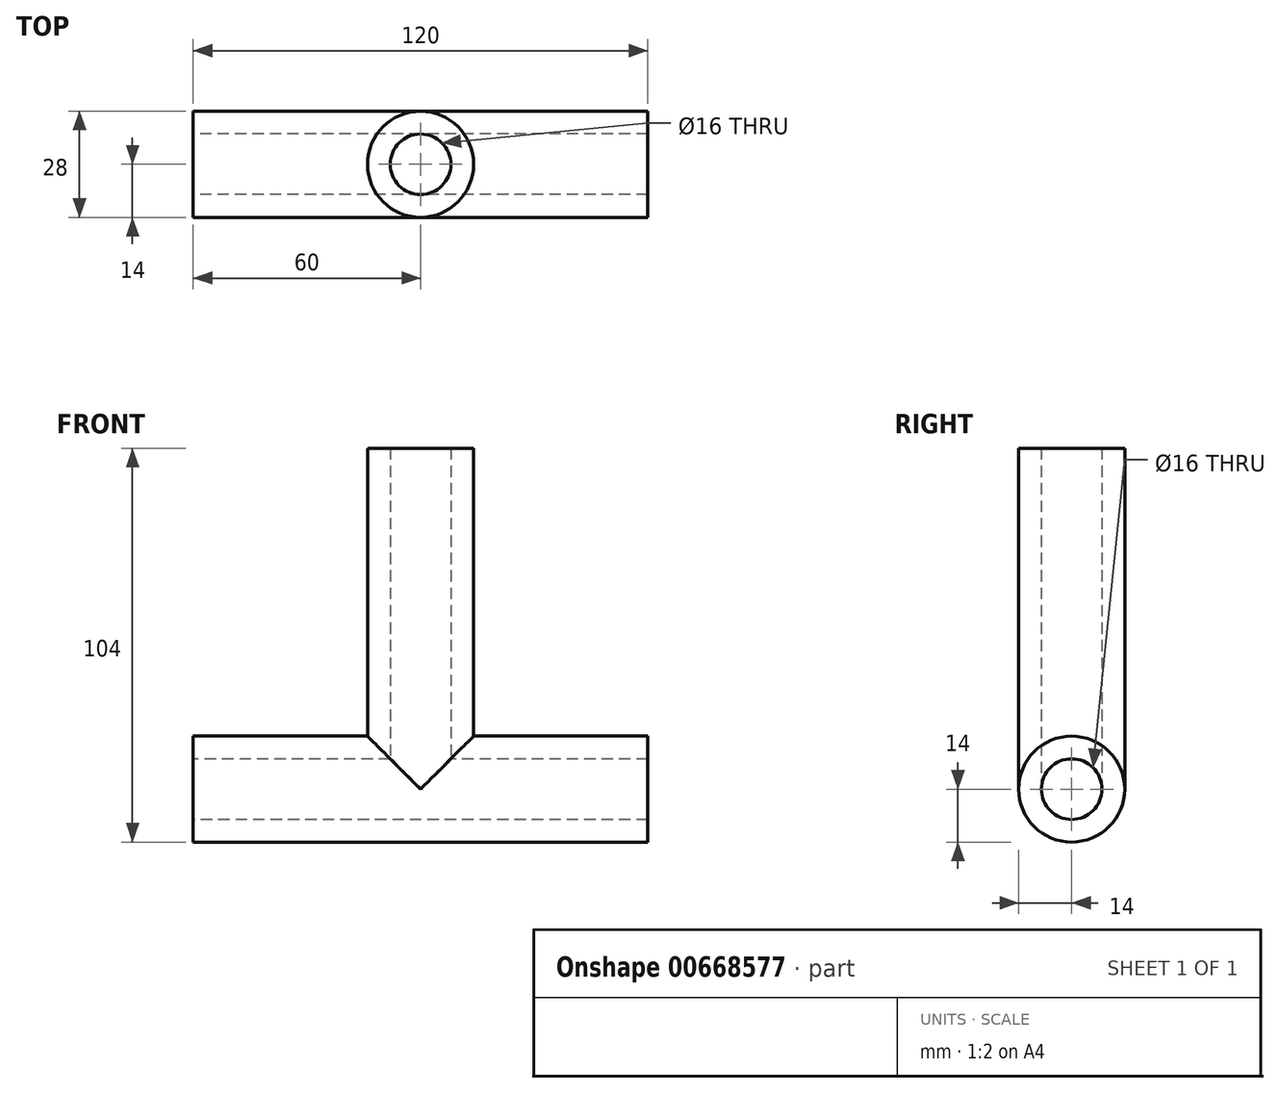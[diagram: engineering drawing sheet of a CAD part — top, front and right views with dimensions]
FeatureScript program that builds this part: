
annotation { "Feature Type Name" : "Feature", "Feature Type Description" : "" }
export const myFeature = defineFeature(function(context is Context, id is Id, definition is map)
    precondition{}
    {
        {
            var Q0;
            Q0=qCreatedBy(makeId("Top.planeOp"),FACE);
            var sketch = newSketch(context, id + "F0", { "sketchPlane" : qUnion([Q0])});
            skCircle(sketch, "E0", {"center": v(0, 0) * mm, "radius": 14 * mm});
            skSolve(sketch);
        }
        {
            var Q0;
            Q0=makeQuery(id+"F0.imprint","IMPRINT",FACE,{"disambiguationData":[TD([[makeQuery(id+"F0.imprint","IMPRINT",EDGE,{"derivedFrom":sQuery(id+"F0.wireOp",EDGE,"E0")}),1.0]])]});
            extrude(context, id + "F1", {"entities" : qUnion([Q0]), "depth" : 90 * mm, "offsetDistance" : 25 * mm});
        }
        {
            var Q0;
            Q0=qCreatedBy(makeId("Right.planeOp"),FACE);
            var sketch = newSketch(context, id + "F2", { "sketchPlane" : qUnion([Q0])});
            skCircle(sketch, "E1", {"center": v(0, 0) * mm, "radius": 14 * mm});
            skSolve(sketch);
        }
        {
            var Q0;
            Q0=makeQuery(id+"F2.imprint","IMPRINT",FACE,{"disambiguationData":[TD([[makeQuery(id+"F2.imprint","IMPRINT",EDGE,{"derivedFrom":sQuery(id+"F2.wireOp",EDGE,"E1")}),1.0]])]});
            extrude(context, id + "F3", {"entities" : qUnion([Q0]), "operationType" : NewBodyOperationType.ADD, "endBound" : BoundingType.SYMMETRIC, "depth" : 120 * mm, "offsetDistance" : 25 * mm});
        }
        {
            var Q0;
            Q0=makeQuery(id+"F1.opExtrude","CAP_FACE",FACE,{"disambiguationData":[OSD([sQuery(id+"F0.wireOp",EDGE,"E0")])],"isStart":false});
            var Q1;
            Q1=makeQuery(id+"F3.opExtrude","CAP_FACE",FACE,{"disambiguationData":[OSD([sQuery(id+"F2.wireOp",EDGE,"E1")])],"isStart":true});
            var Q2;
            Q2=makeQuery(id+"F3.opExtrude","CAP_FACE",FACE,{"disambiguationData":[OSD([sQuery(id+"F2.wireOp",EDGE,"E1")])],"isStart":false});
            shell(context, id + "F4", {"entities" : qUnion([Q0, Q1, Q2]), "thickness" : 6 * mm});
        }
    });
